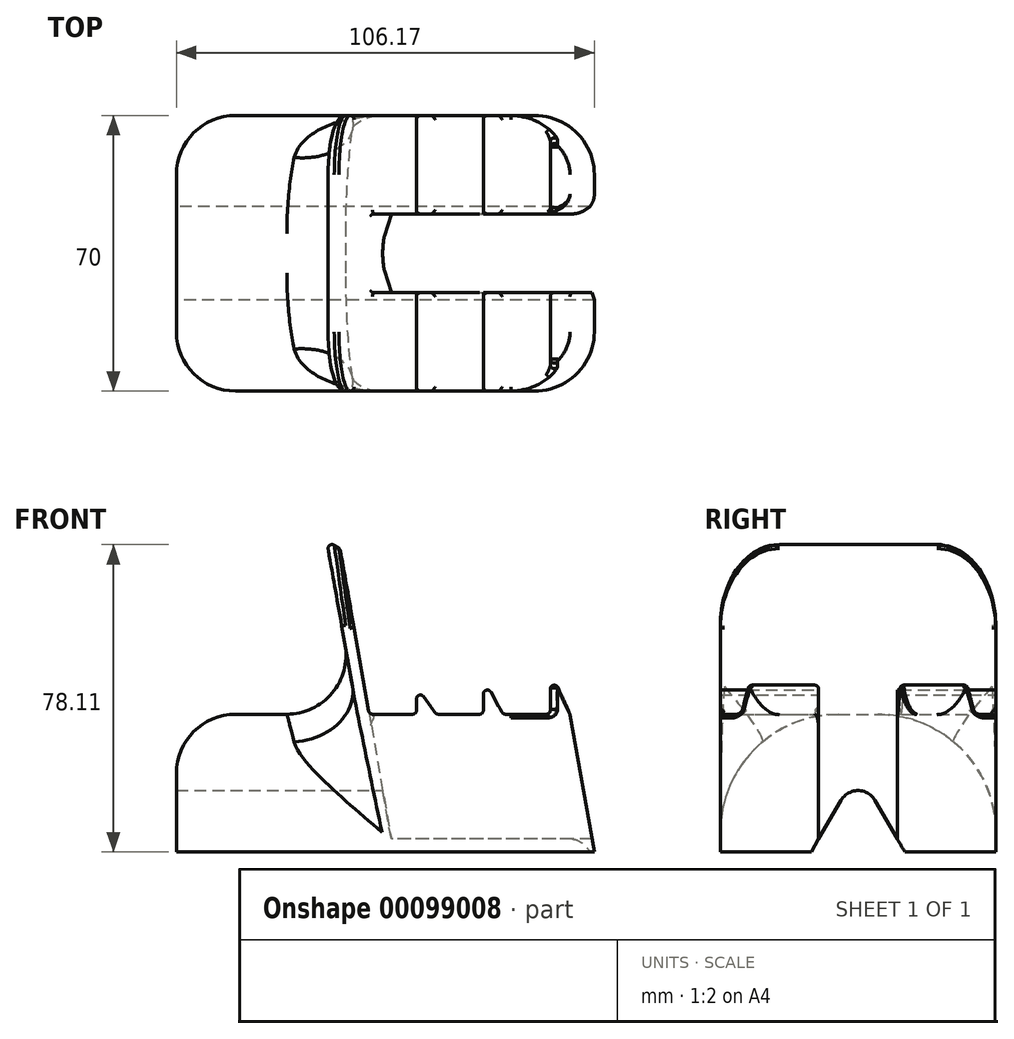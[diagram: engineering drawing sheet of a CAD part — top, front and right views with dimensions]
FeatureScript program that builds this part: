
annotation { "Feature Type Name" : "Feature", "Feature Type Description" : "" }
export const myFeature = defineFeature(function(context is Context, id is Id, definition is map)
    precondition{}
    {
        {
            var Q0;
            Q0=qCreatedBy(makeId("Front.planeOp"),FACE);
            var sketch = newSketch(context, id + "F0", { "sketchPlane" : qUnion([Q0])});
            skLineSegment(sketch, "E0.bottom", {"start": v(-55.17, 35) * mm, "end": v(-9.22, 35) * mm});
            skLineSegment(sketch, "E0.top", {"start": v(-55.17, 0) * mm, "end": v(51, 0) * mm});
            skLineSegment(sketch, "E0.left", {"start": v(-55.17, 35) * mm, "end": v(-55.17, 0) * mm});
            skLineSegment(sketch, "E0.right", {"start": v(44.83, 35) * mm, "end": v(51, 0) * mm});
            skLineSegment(sketch, "E1", {"start": v(-6.17, 35) * mm, "end": v(-13.56, 76.88) * mm});
            skLineSegment(sketch, "E2", {"start": v(-17.03, 79.32) * mm, "end": v(-9.22, 35) * mm});
            skLineSegment(sketch, "E3.top", {"start": v(5.83, 42) * mm, "end": v(11.13, 42) * mm});
            skLineSegment(sketch, "E3.left", {"start": v(5.83, 35) * mm, "end": v(5.83, 42) * mm});
            skLineSegment(sketch, "E4.top", {"start": v(22.83, 44) * mm, "end": v(28.12, 44) * mm});
            skLineSegment(sketch, "E4.left", {"start": v(22.83, 35) * mm, "end": v(22.83, 44) * mm});
            skLineSegment(sketch, "E4.right", {"start": v(27.83, 35) * mm, "end": v(27.83, 35) * mm});
            skLineSegment(sketch, "E5.right", {"start": v(39.83, 35) * mm, "end": v(39.83, 46) * mm});
            skLineSegment(sketch, "E6.trimOffspring", {"start": v(-6.17, 35) * mm, "end": v(5.83, 35) * mm});
            skPoint(sketch, "E7.orphan", {"position": v(0, 0) * mm});
            skLineSegment(sketch, "E8.trimOffspring", {"start": v(10.83, 35) * mm, "end": v(22.83, 35) * mm});
            skLineSegment(sketch, "E9.trimOffspring", {"start": v(27.83, 35) * mm, "end": v(39.83, 35) * mm});
            skLineSegment(sketch, "E10", {"start": v(5.83, 42) * mm, "end": v(10.83, 35) * mm});
            skLineSegment(sketch, "E11", {"start": v(22.83, 44) * mm, "end": v(27.83, 35) * mm});
            skLineSegment(sketch, "E12", {"start": v(39.83, 46) * mm, "end": v(44.83, 35) * mm});
            skLineSegment(sketch, "E13", {"start": v(-17.03, 79.32) * mm, "end": v(-13.56, 76.88) * mm});
            skSolve(sketch);
        }
        {
            var Q0;
            Q0=makeQuery(id+"F0.imprint","IMPRINT",FACE,{"disambiguationData":[TD([[makeQuery(id+"F0.imprint","IMPRINT",EDGE,{"derivedFrom":sQuery(id+"F0.wireOp",EDGE,"E0.bottom")}),-1.0]])]});
            extrude(context, id + "F1", {"entities" : qUnion([Q0]), "endBound" : BoundingType.SYMMETRIC, "depth" : 70 * mm});
        }
        {
            var Q0;
            Q0=makeQuery(id+"F1.opExtrude","SWEPT_FACE",FACE,{"disambiguationData":[OSD([sQuery(id+"F0.wireOp",EDGE,"E0.right")])]});
            var sketch = newSketch(context, id + "F2", { "sketchPlane" : qUnion([Q0])});
            skLineSegment(sketch, "E14.bottom", {"start": v(-10, 40.35) * mm, "end": v(10, 40.35) * mm});
            skLineSegment(sketch, "E14.left", {"start": v(-10, 40.35) * mm, "end": v(-10, -8.86) * mm});
            skLineSegment(sketch, "E14.right", {"start": v(10, 40.35) * mm, "end": v(10, -8.86) * mm});
            skPoint(sketch, "E14.middle", {"position": v(0, -8.86) * mm});
            skLineSegment(sketch, "E15", {"start": v(-10, -8.86) * mm, "end": v(10, -8.86) * mm});
            skSolve(sketch);
        }
        {
            var Q0;
            Q0 = qSketchRegion(id + "F2", true);
            var Q1;
            Q1=makeQuery(id+"F1.opExtrude","SWEPT_FACE",FACE,{"disambiguationData":[OSD([sQuery(id+"F0.wireOp",EDGE,"E1")])]});
            extrude(context, id + "F3", {"entities" : qUnion([Q0]), "operationType" : NewBodyOperationType.REMOVE, "endBound" : BoundingType.UP_TO_SURFACE, "oppositeDirection" : true, "endBoundEntityFace" : qUnion([Q1]), "depth" : 25 * mm});
        }
        {
            var Q0;
            Q0=makeQuery(id+"F1.opExtrude","SWEPT_FACE",FACE,{"disambiguationData":[OSD([sQuery(id+"F0.wireOp",EDGE,"E0.left")])]});
            var sketch = newSketch(context, id + "F4", { "sketchPlane" : qUnion([Q0])});
            skLineSegment(sketch, "E16", {"start": v(0, 0) * mm, "end": v(11.9, 0) * mm});
            skLineSegment(sketch, "E17", {"start": v(11.9, 0) * mm, "end": v(0, 20.6) * mm});
            skLineSegment(sketch, "E18", {"start": v(0, 20.6) * mm, "end": v(-11.9, 0) * mm});
            skLineSegment(sketch, "E19", {"start": v(-11.9, 0) * mm, "end": v(0, 0) * mm});
            skSolve(sketch);
        }
        {
            var Q0;
            Q0=makeQuery(id+"F4.imprint","IMPRINT",FACE,{"disambiguationData":[TD([[makeQuery(id+"F4.imprint","IMPRINT",EDGE,{"derivedFrom":sQuery(id+"F4.wireOp",EDGE,"E16")}),-1.0]])]});
            extrude(context, id + "F5", {"entities" : qUnion([Q0]), "operationType" : NewBodyOperationType.REMOVE, "endBound" : BoundingType.THROUGH_ALL, "oppositeDirection" : true, "depth" : 25 * mm});
        }
        {
            var Q0;
            Q0=makeQuery(id+"F1.opExtrude","CAP_EDGE",EDGE,{"disambiguationData":[OSD([sQuery(id+"F0.wireOp",EDGE,"E13")])],"isStart":false});
            var Q1;
            Q1=makeQuery(id+"F1.opExtrude","CAP_EDGE",EDGE,{"disambiguationData":[OSD([sQuery(id+"F0.wireOp",EDGE,"E13")])],"isStart":true});
            fillet(context, id + "F6", {"entities" : qUnion([Q0, Q1]), "radius" : 15 * mm, "tangentPropagation" : true, "allowEdgeOverflow" : false});
        }
        {
            var Q0;
            Q0=makeQuery(id+"F5.boolean.opBoolean","COPY",EDGE,{"derivedFrom":makeQuery(id+"F5.opExtrude","SWEPT_EDGE",EDGE,{"disambiguationData":[OSD([sQuery(id+"F4.wireOp",EDGE,"E17"),sQuery(id+"F4.wireOp",EDGE,"E18")])]})});
            fillet(context, id + "F7", {"entities" : qUnion([Q0]), "radius" : 5 * mm, "tangentPropagation" : true, "allowEdgeOverflow" : false});
        }
        {
            var Q0;
            Q0=makeQuery(id+"F1.opExtrude","CAP_EDGE",EDGE,{"disambiguationData":[OSD([sQuery(id+"F0.wireOp",EDGE,"E0.right")])],"isStart":false});
            var Q1;
            Q1=makeQuery(id+"F1.opExtrude","CAP_EDGE",EDGE,{"disambiguationData":[OSD([sQuery(id+"F0.wireOp",EDGE,"E0.right")])],"isStart":true});
            fillet(context, id + "F8", {"entities" : qUnion([Q0, Q1]), "radius" : 15 * mm, "tangentPropagation" : true, "allowEdgeOverflow" : false});
        }
        {
            var Q0;
            Q0=makeQuery(id+"F3.boolean.opBoolean","COPY",EDGE,{"derivedFrom":makeQuery(id+"F3.opExtrude","CAP_EDGE",EDGE,{"disambiguationData":[OSD([sQuery(id+"F2.wireOp",EDGE,"E14.left")])],"isStart":true})});
            var Q1;
            Q1=makeQuery(id+"F3.boolean.opBoolean","COPY",EDGE,{"derivedFrom":makeQuery(id+"F3.opExtrude","CAP_EDGE",EDGE,{"disambiguationData":[OSD([sQuery(id+"F2.wireOp",EDGE,"E14.right")])],"isStart":true})});
            fillet(context, id + "F9", {"entities" : qUnion([Q0, Q1]), "radius" : 5 * mm, "tangentPropagation" : true, "allowEdgeOverflow" : false});
        }
        {
            var Q0;
            {var subQ2=sQuery(id+"F0.wireOp",EDGE,"E6.trimOffspring");Q0=makeQuery(id+"F3.boolean.opBoolean","SPLIT",FACE,{"disambiguationData":[TD([makeQuery(id+"F3.opExtrude","SWEPT_FACE",FACE,{"disambiguationData":[OSD([sQuery(id+"F2.wireOp",EDGE,"E14.left")])]})])],"derivedFrom":makeQuery(id+"F1.opExtrude","SWEPT_FACE",FACE,{"disambiguationData":[OSD([subQ2])]})});}
            var Q1;
            {var subQ1=sQuery(id+"F0.wireOp",EDGE,"E8.trimOffspring");Q1=makeQuery(id+"F3.boolean.opBoolean","SPLIT",FACE,{"disambiguationData":[TD([makeQuery(id+"F3.opExtrude","SWEPT_FACE",FACE,{"disambiguationData":[OSD([sQuery(id+"F2.wireOp",EDGE,"E14.left")])]})])],"derivedFrom":makeQuery(id+"F1.opExtrude","SWEPT_FACE",FACE,{"disambiguationData":[OSD([subQ1])]})});}
            var Q2;
            {var subQ1=sQuery(id+"F0.wireOp",EDGE,"E6.trimOffspring");Q2=makeQuery(id+"F3.boolean.opBoolean","SPLIT",FACE,{"disambiguationData":[TD([makeQuery(id+"F3.opExtrude","SWEPT_FACE",FACE,{"disambiguationData":[OSD([sQuery(id+"F2.wireOp",EDGE,"E14.right")])]})])],"derivedFrom":makeQuery(id+"F1.opExtrude","SWEPT_FACE",FACE,{"disambiguationData":[OSD([subQ1])]})});}
            var Q3;
            {var subQ1=sQuery(id+"F0.wireOp",EDGE,"E8.trimOffspring");Q3=makeQuery(id+"F3.boolean.opBoolean","SPLIT",FACE,{"disambiguationData":[TD([makeQuery(id+"F3.opExtrude","SWEPT_FACE",FACE,{"disambiguationData":[OSD([sQuery(id+"F2.wireOp",EDGE,"E14.right")])]})])],"derivedFrom":makeQuery(id+"F1.opExtrude","SWEPT_FACE",FACE,{"disambiguationData":[OSD([subQ1])]})});}
            fillet(context, id + "F10", {"entities" : qUnion([Q0, Q1, Q2, Q3]), "radius" : 1 * mm, "tangentPropagation" : true, "allowEdgeOverflow" : false});
        }
        {
            var Q0;
            Q0=makeQuery(id+"F1.opExtrude","SWEPT_EDGE",EDGE,{"disambiguationData":[OSD([sQuery(id+"F0.wireOp",EDGE,"E3.left"),sQuery(id+"F0.wireOp",EDGE,"8321fb7f-3458-440f-b528-b5414c48c93d.filletArc")])]});
            var Q1;
            Q1=makeQuery(id+"F1.opExtrude","SWEPT_EDGE",EDGE,{"disambiguationData":[OSD([sQuery(id+"F0.wireOp",EDGE,"E4.left"),sQuery(id+"F0.wireOp",EDGE,"d95e2400-caf3-4430-b733-34f4ab988b37.filletArc")])]});
            var Q2;
            Q2=makeQuery(id+"F1.opExtrude","SWEPT_EDGE",EDGE,{"disambiguationData":[OSD([sQuery(id+"F0.wireOp",EDGE,"E5.right"),sQuery(id+"F0.wireOp",EDGE,"e5e4de03-1c67-4efd-834d-6cea7254acc7.filletArc")])]});
            fillet(context, id + "F11", {"entities" : qUnion([Q0, Q1, Q2]), "radius" : 1 * mm, "tangentPropagation" : true, "allowEdgeOverflow" : false});
        }
        {
            var Q0;
            Q0=makeQuery(id+"F1.opExtrude","SWEPT_EDGE",EDGE,{"disambiguationData":[OSD([sQuery(id+"F0.wireOp",EDGE,"E1"),sQuery(id+"F0.wireOp",EDGE,"E13")])]});
            fillet(context, id + "F12", {"entities" : qUnion([Q0]), "radius" : 1 * mm, "tangentPropagation" : true, "allowEdgeOverflow" : false});
        }
        {
            var Q0;
            Q0=makeQuery(id+"F1.opExtrude","CAP_EDGE",EDGE,{"disambiguationData":[OSD([sQuery(id+"F0.wireOp",EDGE,"E0.bottom")])],"isStart":true});
            var Q1;
            Q1=makeQuery(id+"F1.opExtrude","CAP_EDGE",EDGE,{"disambiguationData":[OSD([sQuery(id+"F0.wireOp",EDGE,"E0.bottom")])],"isStart":false});
            fillet(context, id + "F13", {"entities" : qUnion([Q0, Q1]), "radius" : 30 * mm, "tangentPropagation" : true, "allowEdgeOverflow" : false});
        }
        {
            var Q0;
            Q0=makeQuery(id+"F1.opExtrude","CAP_EDGE",EDGE,{"disambiguationData":[OSD([sQuery(id+"F0.wireOp",EDGE,"E2")])],"isStart":true});
            fillet(context, id + "F14", {"entities" : qUnion([Q0]), "radius" : 1 * mm, "tangentPropagation" : true, "allowEdgeOverflow" : false});
        }
        {
            var Q0;
            {var subQ0=sQuery(id+"F0.wireOp",EDGE,"E0.bottom");Q0=makeQuery(id+"F13.opFillet","BLEND_FACE",FACE,{"disambiguationData":[OSD([subQ0]),TDD([makeQuery(id+"F1.opExtrude","CAP_EDGE",EDGE,{"disambiguationData":[OSD([subQ0])],"isStart":true})])]});}
            fillet(context, id + "F15", {"entities" : qUnion([Q0]), "radius" : 15 * mm, "tangentPropagation" : true, "allowEdgeOverflow" : false});
        }
        {
            var Q0;
            {var subQ1=sQuery(id+"F0.wireOp",EDGE,"E9.trimOffspring");Q0=makeQuery(id+"F3.boolean.opBoolean","SPLIT",FACE,{"disambiguationData":[TD([makeQuery(id+"F3.opExtrude","SWEPT_FACE",FACE,{"disambiguationData":[OSD([sQuery(id+"F2.wireOp",EDGE,"E14.left")])]})])],"derivedFrom":makeQuery(id+"F1.opExtrude","SWEPT_FACE",FACE,{"disambiguationData":[OSD([subQ1])]})});}
            var Q1;
            {var subQ1=sQuery(id+"F0.wireOp",EDGE,"E9.trimOffspring");Q1=makeQuery(id+"F3.boolean.opBoolean","SPLIT",FACE,{"disambiguationData":[TD([makeQuery(id+"F3.opExtrude","SWEPT_FACE",FACE,{"disambiguationData":[OSD([sQuery(id+"F2.wireOp",EDGE,"E14.right")])]})])],"derivedFrom":makeQuery(id+"F1.opExtrude","SWEPT_FACE",FACE,{"disambiguationData":[OSD([subQ1])]})});}
            fillet(context, id + "F16", {"entities" : qUnion([Q0, Q1]), "radius" : 1 * mm, "tangentPropagation" : true, "allowEdgeOverflow" : false});
        }
    });
